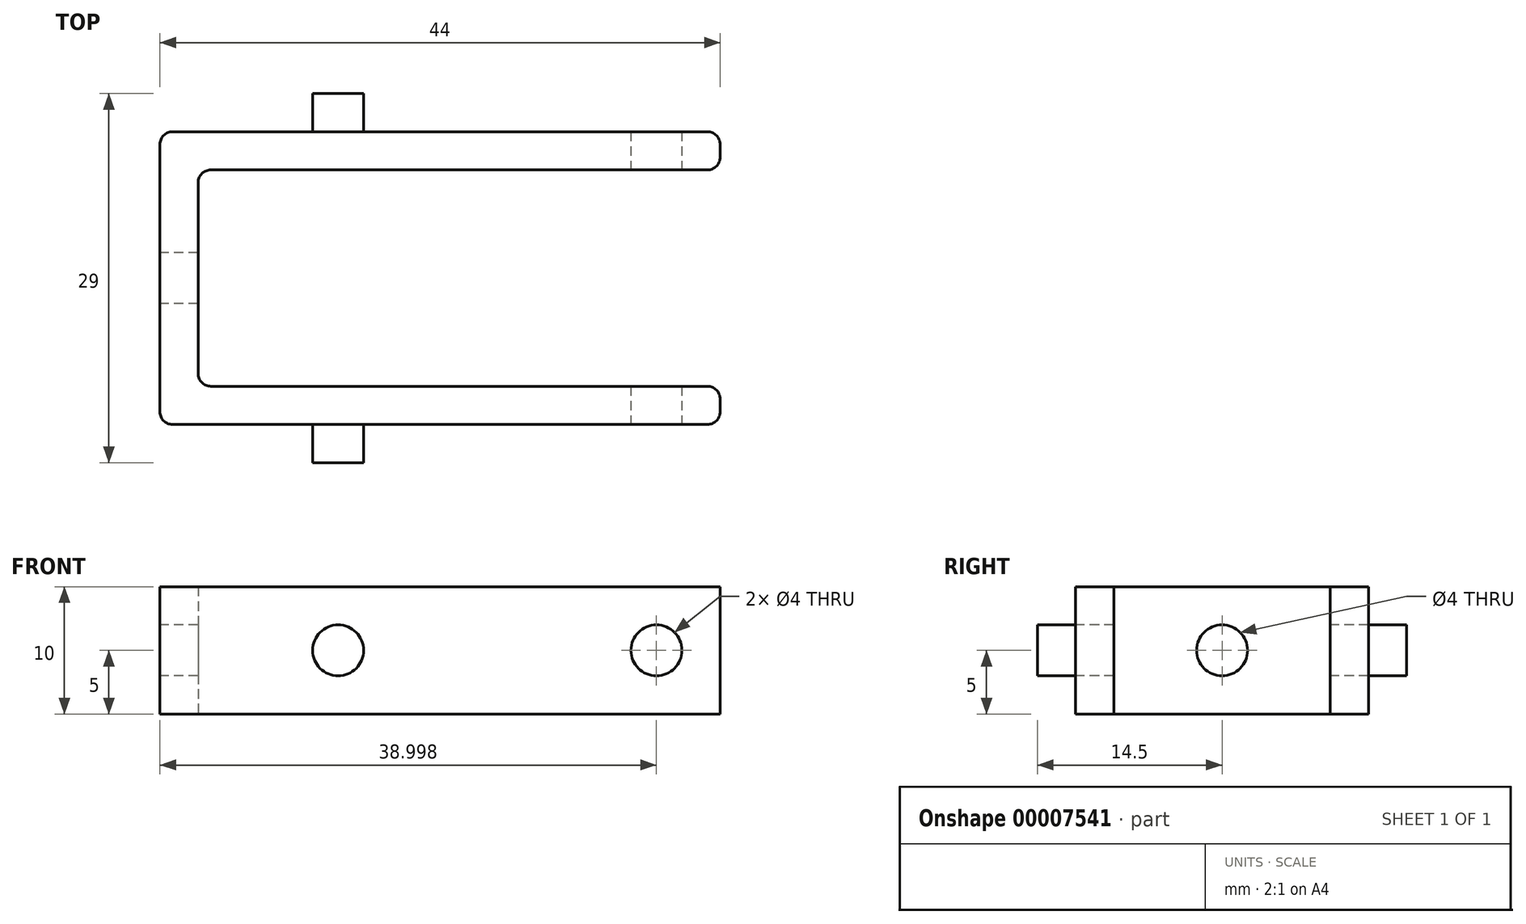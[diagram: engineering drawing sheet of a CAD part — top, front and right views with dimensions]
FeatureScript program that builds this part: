
annotation { "Feature Type Name" : "Feature", "Feature Type Description" : "" }
export const myFeature = defineFeature(function(context is Context, id is Id, definition is map)
    precondition{}
    {
        {
            var Q0;
            Q0=qCreatedBy(makeId("Top.planeOp"),FACE);
            var sketch = newSketch(context, id + "F0", { "sketchPlane" : qUnion([Q0])});
            skLineSegment(sketch, "E0", {"start": v(-20.51, 0) * mm, "end": v(-20.51, 11.5) * mm});
            skLineSegment(sketch, "E1", {"start": v(-20.51, 11.5) * mm, "end": v(23.49, 11.5) * mm});
            skLineSegment(sketch, "E2", {"start": v(23.49, 11.5) * mm, "end": v(23.49, 8.5) * mm});
            skLineSegment(sketch, "E3", {"start": v(23.49, 8.5) * mm, "end": v(-17.51, 8.5) * mm});
            skLineSegment(sketch, "E4", {"start": v(-17.51, 8.5) * mm, "end": v(-17.51, 0) * mm});
            skLineSegment(sketch, "E5.0.MirrorCS", {"start": v(-20.51, 0) * mm, "end": v(-20.51, -11.5) * mm});
            skLineSegment(sketch, "E5.1.MirrorCS", {"start": v(-20.51, -11.5) * mm, "end": v(23.49, -11.5) * mm});
            skLineSegment(sketch, "E5.2.MirrorCS", {"start": v(23.49, -8.5) * mm, "end": v(-17.51, -8.5) * mm});
            skLineSegment(sketch, "E5.3.MirrorCS", {"start": v(-17.51, -8.5) * mm, "end": v(-17.51, 0) * mm});
            skLineSegment(sketch, "E5.4.MirrorCS", {"start": v(23.49, -11.5) * mm, "end": v(23.49, -8.5) * mm});
            skSolve(sketch);
        }
        {
            var Q0;
            Q0 = qSketchRegion(id + "F0", true);
            extrude(context, id + "F1", {"entities" : qUnion([Q0]), "endBound" : BoundingType.SYMMETRIC, "depth" : 10 * mm});
        }
        {
            var Q0;
            Q0=makeQuery(id+"F1.opExtrude","SWEPT_FACE",FACE,{"disambiguationData":[OSD([sQuery(id+"F0.wireOp",EDGE,"E5.1.MirrorCS")])]});
            var sketch = newSketch(context, id + "F2", { "sketchPlane" : qUnion([Q0])});
            skCircle(sketch, "E6", {"center": v(18.49, 0) * mm, "radius": 2 * mm});
            skCircle(sketch, "E7", {"center": v(-6.51, 0) * mm, "radius": 2 * mm});
            skSolve(sketch);
        }
        {
            var Q0;
            Q0=makeQuery(id+"F2.imprint","IMPRINT",FACE,{"disambiguationData":[TD([[makeQuery(id+"F2.imprint","IMPRINT",EDGE,{"derivedFrom":sQuery(id+"F2.wireOp",EDGE,"E6")}),1.0]])]});
            extrude(context, id + "F3", {"entities" : qUnion([Q0]), "operationType" : NewBodyOperationType.REMOVE, "endBound" : BoundingType.THROUGH_ALL, "oppositeDirection" : true, "depth" : 25 * mm});
        }
        {
            var Q0;
            Q0=makeQuery(id+"F1.opExtrude","SWEPT_FACE",FACE,{"disambiguationData":[OSD([sQuery(id+"F0.wireOp",EDGE,"E0"),sQuery(id+"F0.wireOp",EDGE,"E5.0.MirrorCS")])]});
            var sketch = newSketch(context, id + "F4", { "sketchPlane" : qUnion([Q0])});
            skCircle(sketch, "E8", {"center": v(0, 0) * mm, "radius": 2 * mm});
            skSolve(sketch);
        }
        {
            var Q0;
            Q0 = qSketchRegion(id + "F4", true);
            extrude(context, id + "F5", {"entities" : qUnion([Q0]), "operationType" : NewBodyOperationType.REMOVE, "endBound" : BoundingType.THROUGH_ALL, "oppositeDirection" : true, "depth" : 25 * mm});
        }
        {
            var Q0;
            Q0=makeQuery(id+"F2.imprint","IMPRINT",FACE,{"disambiguationData":[TD([[makeQuery(id+"F2.imprint","IMPRINT",EDGE,{"derivedFrom":sQuery(id+"F2.wireOp",EDGE,"E7")}),1.0]])]});
            extrude(context, id + "F6", {"entities" : qUnion([Q0]), "operationType" : NewBodyOperationType.ADD, "depth" : 3 * mm});
        }
        {
            var Q0;
            Q0=makeQuery(id+"F1.opExtrude","SWEPT_FACE",FACE,{"disambiguationData":[OSD([sQuery(id+"F0.wireOp",EDGE,"E1")])]});
            var sketch = newSketch(context, id + "F7", { "sketchPlane" : qUnion([Q0])});
            skCircle(sketch, "E9", {"center": v(6.51, 0) * mm, "radius": 2 * mm});
            skSolve(sketch);
        }
        {
            var Q0;
            Q0 = qSketchRegion(id + "F7", true);
            extrude(context, id + "F8", {"entities" : qUnion([Q0]), "operationType" : NewBodyOperationType.ADD, "depth" : 3 * mm});
        }
        {
            var Q0;
            Q0=makeQuery(id+"F1.opExtrude","SWEPT_EDGE",EDGE,{"disambiguationData":[OSD([sQuery(id+"F0.wireOp",EDGE,"E0"),sQuery(id+"F0.wireOp",EDGE,"E1")])]});
            var Q1;
            Q1=makeQuery(id+"F1.opExtrude","SWEPT_EDGE",EDGE,{"disambiguationData":[OSD([sQuery(id+"F0.wireOp",EDGE,"E5.0.MirrorCS"),sQuery(id+"F0.wireOp",EDGE,"E5.1.MirrorCS")])]});
            var Q2;
            Q2=makeQuery(id+"F1.opExtrude","SWEPT_EDGE",EDGE,{"disambiguationData":[OSD([sQuery(id+"F0.wireOp",EDGE,"E5.1.MirrorCS"),sQuery(id+"F0.wireOp",EDGE,"E5.4.MirrorCS")])]});
            var Q3;
            Q3=makeQuery(id+"F1.opExtrude","SWEPT_EDGE",EDGE,{"disambiguationData":[OSD([sQuery(id+"F0.wireOp",EDGE,"E1"),sQuery(id+"F0.wireOp",EDGE,"E2")])]});
            var Q4;
            Q4=makeQuery(id+"F1.opExtrude","SWEPT_EDGE",EDGE,{"disambiguationData":[OSD([sQuery(id+"F0.wireOp",EDGE,"E5.2.MirrorCS"),sQuery(id+"F0.wireOp",EDGE,"E5.4.MirrorCS")])]});
            var Q5;
            Q5=makeQuery(id+"F1.opExtrude","SWEPT_EDGE",EDGE,{"disambiguationData":[OSD([sQuery(id+"F0.wireOp",EDGE,"E2"),sQuery(id+"F0.wireOp",EDGE,"E3")])]});
            var Q6;
            Q6=makeQuery(id+"F1.opExtrude","SWEPT_EDGE",EDGE,{"disambiguationData":[OSD([sQuery(id+"F0.wireOp",EDGE,"E5.2.MirrorCS"),sQuery(id+"F0.wireOp",EDGE,"E5.3.MirrorCS")])]});
            var Q7;
            Q7=makeQuery(id+"F1.opExtrude","SWEPT_EDGE",EDGE,{"disambiguationData":[OSD([sQuery(id+"F0.wireOp",EDGE,"E3"),sQuery(id+"F0.wireOp",EDGE,"E4")])]});
            fillet(context, id + "F9", {"entities" : qUnion([Q0, Q1, Q2, Q3, Q4, Q5, Q6, Q7]), "radius" : 1 * mm, "tangentPropagation" : true, "allowEdgeOverflow" : false});
        }
    });
